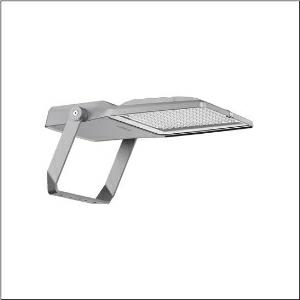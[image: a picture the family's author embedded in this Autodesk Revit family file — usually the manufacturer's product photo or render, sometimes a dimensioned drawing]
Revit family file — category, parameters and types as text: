
# Revit family: floodlight_fl_21_midi___pl61_5xa7786e4c1a_1b6e
name_source: partatom
category: Lighting Fixtures
units: mm (PartAtom-declared; Revit-internal decimal feet)

## family parameters
Cut with Voids When Loaded = No
Host = Face
Light Source = No
Part Type = Normal
Room Calculation Point = No
Round Connector Dimension = Use Diameter
Shared = No

## types (1)
- --- (1 x LED, 27590 lm, 212.4 W, 4000K)
    Apparent Load = 212 VA
    CIE Flux Codes = 33 65 98 100 100
    Color Rendering = 70
    Color Temperature = 4000K
    Default Elevation = 1800 mm
    Description = Floodlight FL 21 midi, floodlight, primary light control with lens, of PMMA, primary optical cover: protective disc, of toughened safety glass, transparent, light distribution: PL61, light emission: direct distribution, installation type: surface-mounted, LED, High Power LED, rated luminous flux: 27.590lm, luminous efficacy: 130lm/W, light colour: 740, colour temperature: 4000K, control gear: Smart Interface (Zhaga)D4i, control: overheat protection, constant luminous flux control, time-dependent luminous flux control, flexible luminous flux parameterisation, pre-setting: logarithmic dimming characteristic, with terminal, 6-pole, mains connection: 220..240V, AC, 50/60Hz, start of lifetime: 212W, end of service life: 231W, reduction: 95W, mounting bracket, of diecast aluminium, powder-coated, Siteco® metallic grey (DB 702S), corrosivity category C5 mid according to DIN EN ISO 12944, suitable for swimming pools, chlorine-resistant, sealing non-destructively replaceable, mounting bracket, of steel, galvanised, powder-coated, Siteco® metallic grey (DB 702S), Smart Interface below and above, protection rating (complete): IP66, insulation class (complete): insulation class II (safety insulation), certification: CE, ENEC, VDE, protection symbol: D, impact resistance: IK08, permissible operating ambient temperature: -40..+40°C, permissible operating ambient temperature for outdoor applications: -40..+50°C, standard: DIN EN 12944, LABS conformity tested according to VDMA 24364:2018-05, packaging unit: 1 piece

Light Distribution: PL61
    Height = 76 mm
    Lamp = 1 x LED
    Lamp Light Flux = 27590 lm
    Lamp Power = 212.4 W
    Lamp count = 1
    Length = 657 mm
    Luminous efficacy = 130 lm/W
    Manufacturer = Siteco
    ModVariant = No
    Model = 5XA7786E4C1A
    Number of Poles = 1
    OnlyDefault = Yes
    Power Factor = 1
    Product Name = Floodlight FL 21 midi | PL61
    Product group = floodlight | pylon annexe
    ProductGroupID = 6200
    Protection Class = Protection class II
    Protection Degree = IP 66
    RLX_Detail_Level = 1
    RLX_Emergency_Light_Flux = 0 lm
    RLX_Emergency_Type = 0
    RLX_Emergency_Type_DB = No
    RlxData = <blob elided: 101805 chars, md5=61bd3544>
    Socket = socket
    Standby Power = 0 W
    System Light Flux = 27590 lm
    System Power = 212 W
    Type Comments = factory setting: luminous flux: 100 % | dim-lin: 254 | 710 mA
    Type Image = l_1006876.jpg
    URL = http://relux.com
    VarID = @adj_090470
    Voltage = 0 V
    Weight = 0.00 kg
    Width = 442 mm

## geometry (parser evidence)
native form markers: Blend x4, Sweep x12
no freeform markers — native parametric forms only
